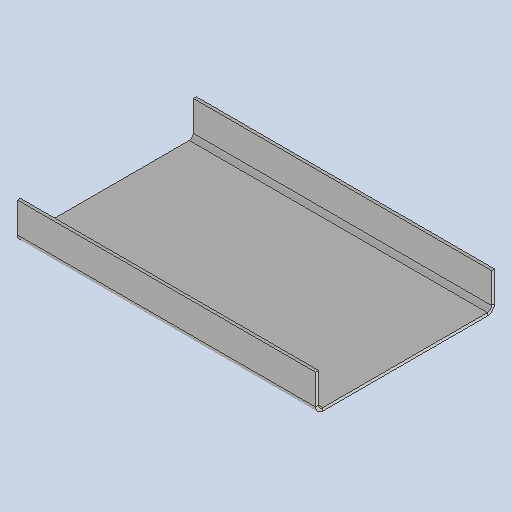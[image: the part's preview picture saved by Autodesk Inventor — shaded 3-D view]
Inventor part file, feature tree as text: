
AUTODESK INVENTOR PART (.ipt)
format: ipt  version: 2025 (Build 290162010, 162A)  size: 245,760 bytes
history: native  units: mm
features: other x5, sheet_metal_op x4, sketch x3
ambient origin geometry x8: Origin, YZ Plane, XZ Plane, XY Plane, X Axis, Y Axis, Z Axis, Center Point
bodies: Solid1 (feature_tree)
feature tree (12):
  sheet_metal_op  "Face1"
  other  "Mark1"
  other  "A-Side Definition"
  sheet_metal_op  "Flange1"
  sketch  "Sketch1"  dims[d0=200.0mm]
  other  "Plate1"
  sketch  "Sketch2"  dims[d1=120.0mm]
  sketch  "Sketch3"  dims[d2=2.0mm d6=200.0mm d9=20.0mm d10=20.0mm d11=20.0mm d12=2.0mm d13=1.0mm d14=4.0mm d15=2.75mm d16=25.0mm d17=90.0deg d18=2.75mm d19=8.0mm d20=2.0mm d21=2.75mm]
  other  "Plate2"
  sheet_metal_op  "Bend1"
  sheet_metal_op  "Corner1"
  other  "Definition1"
